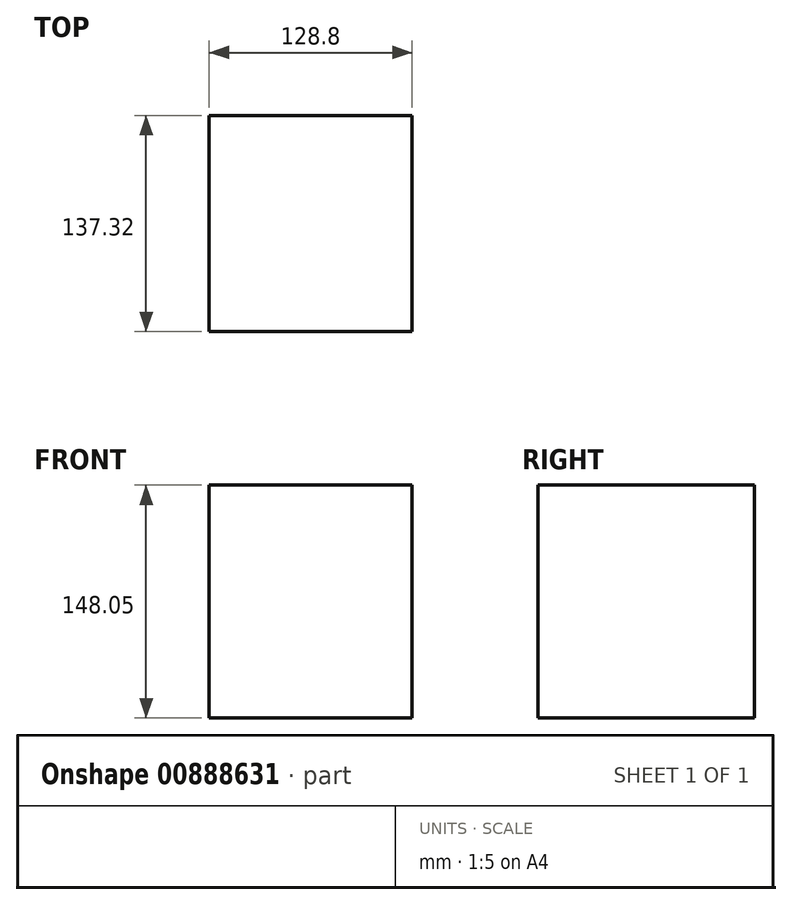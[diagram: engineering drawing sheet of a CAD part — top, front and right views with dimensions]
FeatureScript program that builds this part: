
annotation { "Feature Type Name" : "Feature", "Feature Type Description" : "" }
export const myFeature = defineFeature(function(context is Context, id is Id, definition is map)
    precondition{}
    {
        {
            var Q0;
            Q0=qCreatedBy(makeId("Top.planeOp"),FACE);
            var sketch = newSketch(context, id + "F0", { "sketchPlane" : qUnion([Q0])});
            skLineSegment(sketch, "E0.bottom", {"start": v(68.34, 70.12) * mm, "end": v(-60.46, 70.12) * mm});
            skLineSegment(sketch, "E0.top", {"start": v(68.34, -67.2) * mm, "end": v(-60.46, -67.2) * mm});
            skLineSegment(sketch, "E0.left", {"start": v(68.34, 70.12) * mm, "end": v(68.34, -67.2) * mm});
            skLineSegment(sketch, "E0.right", {"start": v(-60.46, 70.12) * mm, "end": v(-60.46, -67.2) * mm});
            skLineSegment(sketch, "E1.bottom", {"start": v(68.34, -16.87) * mm, "end": v(-60.46, -16.87) * mm, "construction": true});
            skLineSegment(sketch, "E1.top", {"start": v(68.34, 1.46) * mm, "end": v(-60.46, 1.46) * mm, "construction": true});
            skLineSegment(sketch, "E1.left", {"start": v(68.34, -16.87) * mm, "end": v(68.34, 1.46) * mm, "construction": true});
            skLineSegment(sketch, "E1.right", {"start": v(-60.46, -16.87) * mm, "end": v(-60.46, 1.46) * mm, "construction": true});
            skSolve(sketch);
        }
        {
            var Q0;
            Q0=makeQuery(id+"F0.imprint","IMPRINT",FACE,{"disambiguationData":[TD([[makeQuery(id+"F0.imprint","IMPRINT",EDGE,{"derivedFrom":sQuery(id+"F0.wireOp",EDGE,"E0.bottom")}),1.0]])]});
            var sketch = newSketch(context, id + "F1", { "sketchPlane" : qUnion([Q0])});
            skSolve(sketch);
        }
        {
            var Q0;
            Q0=makeQuery(id+"F1.imprint","IMPRINT",FACE,{"disambiguationData":[TD([[makeQuery(id+"F1.imprint","IMPRINT",EDGE,{"derivedFrom":makeQuery(id+"F0.imprint","IMPRINT",EDGE,{"derivedFrom":sQuery(id+"F0.wireOp",EDGE,"E0.bottom")})}),1.0]])]});
            extrude(context, id + "F2", {"entities" : qUnion([Q0]), "depth" : 148.05 * mm, "offsetDistance" : 25.4 * mm});
        }
    });
